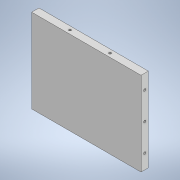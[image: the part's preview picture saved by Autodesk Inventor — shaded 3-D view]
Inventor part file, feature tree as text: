
AUTODESK INVENTOR PART (.ipt)
format: ipt  version: 2022.2 (Build 262287030, 287C)  size: 129,536 bytes
history: native  units: in
note: dims shown in document units (in); Inventor stores cm internally (conversion verified against a paired STEP export)
features: sketch x5, hole x4, extrude x1
ambient origin geometry x8: Origin, YZ Plane, XZ Plane, XY Plane, X Axis, Y Axis, Z Axis, Center Point
bodies: Solid1 (feature_tree)
feature tree (10):
  extrude  "Extrusion1"  Depth=4.5276in
  hole  "Hole1"  [1 undecoded]
  hole  "Hole2"  [1 undecoded]
  hole  "Hole3"  [1 undecoded]
  hole  "Hole4"  [1 undecoded]
  sketch  "Sketch1"  dims[d0=5.9055in d1=4.5276in]
  sketch  "Sketch2"  dims[d2=0.3937in d3=0.0in d4=0.7874in]
  sketch  "Sketch3"  dims[d5=0.1969in d6=1.1811in d8=1.4764in d9=0.3937in d11=0.3937in]
  sketch  "Sketch4"  dims[d13=0.125in d14=0.2953in d15=0.1476in d16=0.0984in d17=90.0deg d18=0.1969in d19=0.0in d20=1.8701in]
  sketch  "Sketch5"  dims[d21=0.1969in d22=0.7874in d24=2.1654in d25=0.3937in d27=0.3937in d29=0.125in d30=0.2953in d31=0.1476in d32=0.0984in d33=90.0deg d34=0.1969in d35=0.0in d36=1.8701in d37=0.1969in d38=0.7874in d40=2.1654in d41=0.3937in d43=0.3937in d45=0.125in d46=0.2953in d47=0.1476in d48=0.0984in d49=90.0deg d50=0.1969in d51=0.0in d52=0.7874in d53=0.1969in d54=1.1811in d56=1.4764in d57=0.3937in d59=0.3937in d61=0.125in d62=0.2953in d63=0.1476in d64=0.0984in d65=90.0deg d66=0.1969in d67=0.0in]
note: 4 required parameter values undecoded (feature->parameter linkage not recoverable at this tier; creation-order binding heuristic only, values carry confidence <= 0.55)
